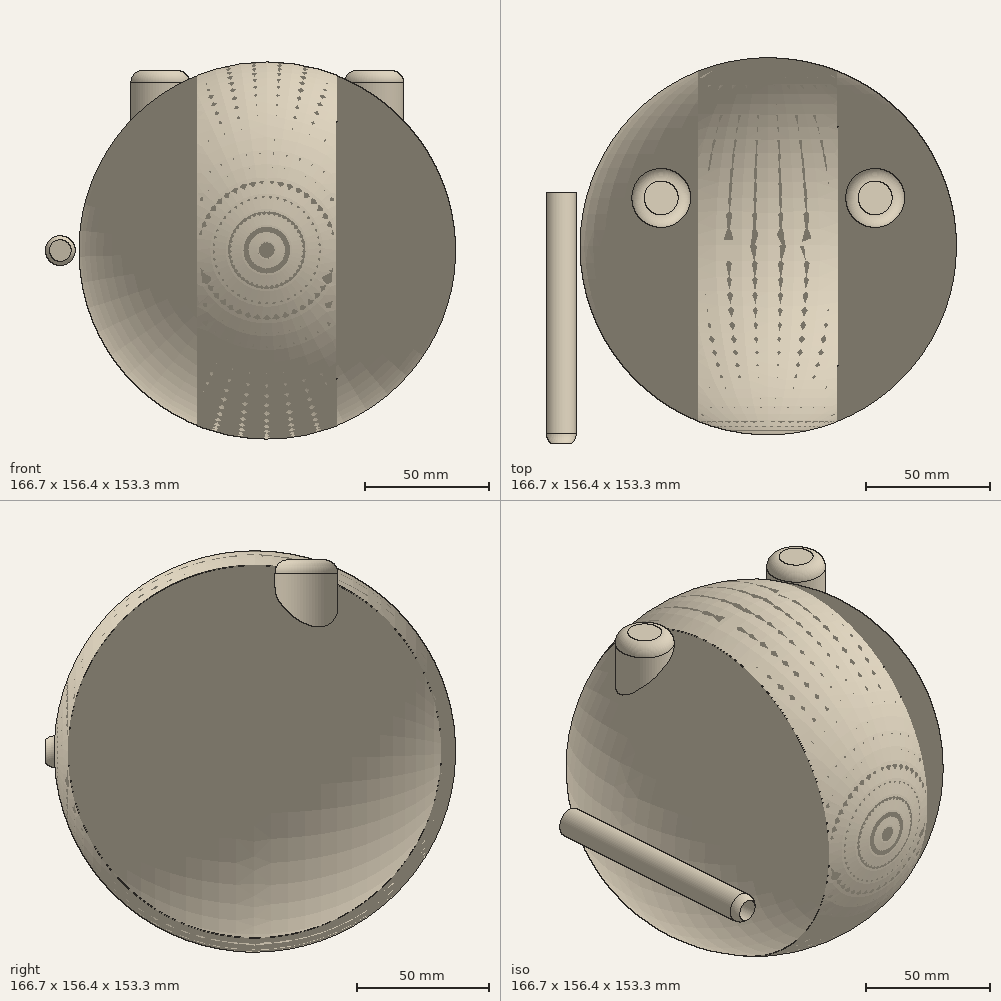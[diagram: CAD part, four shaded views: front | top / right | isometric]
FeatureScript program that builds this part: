
annotation { "Feature Type Name" : "Feature", "Feature Type Description" : "" }
export const myFeature = defineFeature(function(context is Context, id is Id, definition is map)
    precondition{}
    {
        {
            var Q0;
            Q0=qCreatedBy(makeId("Right.planeOp"),FACE);
            var sketch = newSketch(context, id + "F0", { "sketchPlane" : qUnion([Q0])});
            skLineSegment(sketch, "E0", {"start": v(-76.56, 0) * mm, "end": v(76.56, 0) * mm});
            skArc(sketch, "E1", {"start": v(76.56, 0) * mm, "mid": v(0, 76.63) * mm, "end": v(-76.56, 0) * mm});
            skSolve(sketch);
        }
        {
            var Q0;
            Q0=makeQuery(id+"F0.imprint","IMPRINT",FACE,{"disambiguationData":[TD([[makeQuery(id+"F0.imprint","IMPRINT",EDGE,{"derivedFrom":sQuery(id+"F0.wireOp",EDGE,"E0")}),1.0]])]});
            var Q1;
            Q1=sQuery(id+"F0.wireOp",EDGE,"E0");
            revolve(context, id + "F1", {"entities" : qUnion([Q0]), "axis" : qUnion([Q1]), "revolveType" : RevolveType.FULL});
        }
        {
            var Q0;
            Q0=qCreatedBy(makeId("Right.planeOp"),FACE);
            var sketch = newSketch(context, id + "F2", { "sketchPlane" : qUnion([Q0])});
            skCircle(sketch, "E2", {"center": v(0, 0) * mm, "radius": 71.19 * mm});
            skSolve(sketch);
        }
        {
            var Q0;
            Q0 = qSketchRegion(id + "F2", true);
            extrude(context, id + "F3", {"entities" : qUnion([Q0]), "operationType" : NewBodyOperationType.REMOVE, "endBound" : BoundingType.SYMMETRIC, "oppositeDirection" : true, "depth" : 195.07 * mm});
        }
        {
            var Q0;
            Q0=qCreatedBy(makeId("Right.planeOp"),FACE);
            var sketch = newSketch(context, id + "F4", { "sketchPlane" : qUnion([Q0])});
            skCircle(sketch, "E3.0", {"center": v(0, 0) * mm, "radius": 71.19 * mm});
            skCircle(sketch, "E4", {"center": v(0, 0) * mm, "radius": 71.16 * mm});
            skCircle(sketch, "E5", {"center": v(0, 0) * mm, "radius": 65.17 * mm});
            skSolve(sketch);
        }
        {
            var Q0;
            Q0=makeQuery(id+"F4.imprint","IMPRINT",FACE,{"disambiguationData":[TD([[makeQuery(id+"F4.imprint","IMPRINT",EDGE,{"derivedFrom":sQuery(id+"F4.wireOp",EDGE,"E4")}),1.0]])]});
            extrude(context, id + "F5", {"entities" : qUnion([Q0]), "endBound" : BoundingType.SYMMETRIC, "depth" : 56.5 * mm});
        }
        {
            var Q0;
            Q0=qCreatedBy(makeId("Right.planeOp"),FACE);
            var sketch = newSketch(context, id + "F6", { "sketchPlane" : qUnion([Q0])});
            skLineSegment(sketch, "E6", {"start": v(-76.44, 0) * mm, "end": v(76.44, 0) * mm});
            skArc(sketch, "E7", {"start": v(76.44, 0) * mm, "mid": v(0, 75.8) * mm, "end": v(-76.44, 0) * mm});
            skSolve(sketch);
        }
        {
            var Q0;
            Q0=makeQuery(id+"F6.imprint","IMPRINT",FACE,{"disambiguationData":[TD([[makeQuery(id+"F6.imprint","IMPRINT",EDGE,{"derivedFrom":sQuery(id+"F6.wireOp",EDGE,"E6")}),1.0]])]});
            var Q1;
            Q1=sQuery(id+"F6.wireOp",EDGE,"E6");
            revolve(context, id + "F7", {"entities" : qUnion([Q0]), "axis" : qUnion([Q1]), "revolveType" : RevolveType.FULL, "oppositeDirection" : true});
        }
        {
            var Q0;
            Q0=qCreatedBy(makeId("Right.planeOp"),FACE);
            var sketch = newSketch(context, id + "F8", { "sketchPlane" : qUnion([Q0])});
            skLineSegment(sketch, "E8", {"start": v(0, 0) * mm, "end": v(-36.95, 0) * mm});
            skLineSegment(sketch, "E9", {"start": v(-36.95, 0) * mm, "end": v(-36.95, 19.05) * mm});
            skLineSegment(sketch, "E10", {"start": v(-36.95, 19.05) * mm, "end": v(0, 19.05) * mm});
            skLineSegment(sketch, "E11", {"start": v(0, 19.05) * mm, "end": v(0, 0) * mm});
            skLineSegment(sketch, "E12", {"start": v(0, 0) * mm, "end": v(0, -19.05) * mm});
            skLineSegment(sketch, "E13", {"start": v(0, -19.05) * mm, "end": v(-36.95, -19.05) * mm});
            skLineSegment(sketch, "E14", {"start": v(-36.95, -19.05) * mm, "end": v(-36.95, 0) * mm});
            skArc(sketch, "E15", {"start": v(0, -19.05) * mm, "mid": v(44.13, 0) * mm, "end": v(0, 19.05) * mm});
            skSolve(sketch);
        }
        {
            var Q0;
            Q0 = qSketchRegion(id + "F8", true);
            extrude(context, id + "F9", {"entities" : qUnion([Q0]), "operationType" : NewBodyOperationType.ADD, "endBound" : BoundingType.SYMMETRIC, "depth" : 151.9 * mm});
        }
        {
            var Q0;
            {var subQ0=sQuery(id+"F8.wireOp",EDGE,"E14");var subQ1=sQuery(id+"F8.wireOp",EDGE,"E9");var subQ2=sQuery(id+"F8.wireOp",EDGE,"E10");Q0=makeQuery(id+"F9.boolean.opBoolean","SPLIT",EDGE,{"disambiguationData":[TD([makeQuery(id+"F9.opExtrude","CAP_FACE",FACE,{"disambiguationData":[OSD([subQ1,subQ2,sQuery(id+"F8.wireOp",EDGE,"E13"),subQ0,sQuery(id+"F8.wireOp",EDGE,"E15")])],"isStart":false})])],"derivedFrom":makeQuery(id+"F9.opExtrude","SWEPT_EDGE",EDGE,{"disambiguationData":[OSD([subQ1,subQ2])]})});}
            var Q1;
            {var subQ0=sQuery(id+"F8.wireOp",EDGE,"E14");var subQ1=sQuery(id+"F8.wireOp",EDGE,"E9");var subQ2=sQuery(id+"F8.wireOp",EDGE,"E13");Q1=makeQuery(id+"F9.boolean.opBoolean","SPLIT",EDGE,{"disambiguationData":[TD([makeQuery(id+"F9.opExtrude","CAP_FACE",FACE,{"disambiguationData":[OSD([subQ1,sQuery(id+"F8.wireOp",EDGE,"E10"),subQ2,subQ0,sQuery(id+"F8.wireOp",EDGE,"E15")])],"isStart":false})])],"derivedFrom":makeQuery(id+"F9.opExtrude","SWEPT_EDGE",EDGE,{"disambiguationData":[OSD([subQ2,subQ0])]})});}
            var Q2;
            Q2=makeQuery(id+"F9.opExtrude","CAP_EDGE",EDGE,{"disambiguationData":[OSD([sQuery(id+"F8.wireOp",EDGE,"E9"),sQuery(id+"F8.wireOp",EDGE,"E14")])],"isStart":false});
            var Q3;
            Q3=makeQuery(id+"F9.opExtrude","CAP_EDGE",EDGE,{"disambiguationData":[OSD([sQuery(id+"F8.wireOp",EDGE,"E13")])],"isStart":false});
            var Q4;
            Q4=makeQuery(id+"F9.opExtrude","CAP_EDGE",EDGE,{"disambiguationData":[OSD([sQuery(id+"F8.wireOp",EDGE,"E10")])],"isStart":false});
            var Q5;
            Q5=makeQuery(id+"F9.opExtrude","CAP_EDGE",EDGE,{"disambiguationData":[OSD([sQuery(id+"F8.wireOp",EDGE,"E15")])],"isStart":false});
            fillet(context, id + "F10", {"entities" : qUnion([Q0, Q1, Q2, Q3, Q4, Q5]), "radius" : 7.87 * mm, "tangentPropagation" : true, "allowEdgeOverflow" : false});
        }
        {
            var Q0;
            Q0=makeQuery(id+"F9.opExtrude","CAP_EDGE",EDGE,{"disambiguationData":[OSD([sQuery(id+"F8.wireOp",EDGE,"E9"),sQuery(id+"F8.wireOp",EDGE,"E14")])],"isStart":true});
            var Q1;
            {var subQ0=sQuery(id+"F8.wireOp",EDGE,"E14");var subQ1=sQuery(id+"F8.wireOp",EDGE,"E9");var subQ2=sQuery(id+"F8.wireOp",EDGE,"E10");Q1=makeQuery(id+"F9.boolean.opBoolean","SPLIT",EDGE,{"disambiguationData":[TD([makeQuery(id+"F9.opExtrude","CAP_FACE",FACE,{"disambiguationData":[OSD([subQ1,subQ2,sQuery(id+"F8.wireOp",EDGE,"E13"),subQ0,sQuery(id+"F8.wireOp",EDGE,"E15")])],"isStart":true})])],"derivedFrom":makeQuery(id+"F9.opExtrude","SWEPT_EDGE",EDGE,{"disambiguationData":[OSD([subQ1,subQ2])]})});}
            var Q2;
            {var subQ0=sQuery(id+"F8.wireOp",EDGE,"E14");var subQ1=sQuery(id+"F8.wireOp",EDGE,"E9");var subQ2=sQuery(id+"F8.wireOp",EDGE,"E13");Q2=makeQuery(id+"F9.boolean.opBoolean","SPLIT",EDGE,{"disambiguationData":[TD([makeQuery(id+"F9.opExtrude","CAP_FACE",FACE,{"disambiguationData":[OSD([subQ1,sQuery(id+"F8.wireOp",EDGE,"E10"),subQ2,subQ0,sQuery(id+"F8.wireOp",EDGE,"E15")])],"isStart":true})])],"derivedFrom":makeQuery(id+"F9.opExtrude","SWEPT_EDGE",EDGE,{"disambiguationData":[OSD([subQ2,subQ0])]})});}
            var Q3;
            Q3=makeQuery(id+"F9.opExtrude","CAP_EDGE",EDGE,{"disambiguationData":[OSD([sQuery(id+"F8.wireOp",EDGE,"E13")])],"isStart":true});
            var Q4;
            Q4=makeQuery(id+"F9.opExtrude","CAP_EDGE",EDGE,{"disambiguationData":[OSD([sQuery(id+"F8.wireOp",EDGE,"E10")])],"isStart":true});
            var Q5;
            Q5=makeQuery(id+"F9.opExtrude","CAP_EDGE",EDGE,{"disambiguationData":[OSD([sQuery(id+"F8.wireOp",EDGE,"E15")])],"isStart":true});
            fillet(context, id + "F11", {"entities" : qUnion([Q0, Q1, Q2, Q3, Q4, Q5]), "radius" : 7.87 * mm, "tangentPropagation" : true, "allowEdgeOverflow" : false});
        }
        {
            var Q0;
            Q0=makeQuery(id+"F9.opExtrude","CAP_FACE",FACE,{"disambiguationData":[OSD([sQuery(id+"F8.wireOp",EDGE,"E9"),sQuery(id+"F8.wireOp",EDGE,"E10"),sQuery(id+"F8.wireOp",EDGE,"E13"),sQuery(id+"F8.wireOp",EDGE,"E14"),sQuery(id+"F8.wireOp",EDGE,"E15")])],"isStart":false});
            var sketch = newSketch(context, id + "F12", { "sketchPlane" : qUnion([Q0])});
            skLineSegment(sketch, "E16", {"start": v(-29.07, 0) * mm, "end": v(36.26, 0) * mm});
            skLineSegment(sketch, "E17", {"start": v(0, 0) * mm, "end": v(0, 13.22) * mm});
            skLineSegment(sketch, "E18", {"start": v(0, 0) * mm, "end": v(0, -13.22) * mm});
            skArc(sketch, "E19", {"start": v(20.06, -18.18) * mm, "mid": v(36.26, 0) * mm, "end": v(20.06, 18.18) * mm});
            skLineSegment(sketch, "E20", {"start": v(20.06, 18.18) * mm, "end": v(20.06, -18.18) * mm});
            skSolve(sketch);
        }
        {
            var Q0;
            {var subQ0=sQuery(id+"F12.wireOp",EDGE,"E19");var subQ1=sQuery(id+"F12.wireOp",EDGE,"E16");var subQ2=makeQuery(id+"F12.imprint","INTERSECT",VERTEX,{"derivedFrom":[subQ1,subQ0]});Q0=makeQuery(id+"F12.imprint","IMPRINT",FACE,{"disambiguationData":[TD([[makeQuery(id+"F12.imprint","IMPRINT",EDGE,{"disambiguationData":[TD([[subQ2,1.0]])],"derivedFrom":subQ1}),1.0]])]});}
            var Q1;
            {var subQ0=sQuery(id+"F12.wireOp",EDGE,"E19");var subQ1=sQuery(id+"F12.wireOp",EDGE,"E16");var subQ2=makeQuery(id+"F12.imprint","INTERSECT",VERTEX,{"derivedFrom":[subQ1,subQ0]});Q1=makeQuery(id+"F12.imprint","IMPRINT",FACE,{"disambiguationData":[TD([[makeQuery(id+"F12.imprint","IMPRINT",EDGE,{"disambiguationData":[TD([[subQ2,1.0]])],"derivedFrom":subQ1}),-1.0]])]});}
            var Q2;
            Q2=sQuery(id+"F12.wireOp",EDGE,"E20");
            revolve(context, id + "F13", {"operationType" : NewBodyOperationType.ADD, "entities" : qUnion([Q0, Q1]), "axis" : qUnion([Q2]), "revolveType" : RevolveType.FULL});
        }
        {
            var Q0;
            Q0=makeQuery(id+"F9.opExtrude","CAP_FACE",FACE,{"disambiguationData":[OSD([sQuery(id+"F8.wireOp",EDGE,"E9"),sQuery(id+"F8.wireOp",EDGE,"E10"),sQuery(id+"F8.wireOp",EDGE,"E13"),sQuery(id+"F8.wireOp",EDGE,"E14"),sQuery(id+"F8.wireOp",EDGE,"E15")])],"isStart":true});
            var sketch = newSketch(context, id + "F14", { "sketchPlane" : qUnion([Q0])});
            skLineSegment(sketch, "E21", {"start": v(0, 0) * mm, "end": v(29.07, 0) * mm});
            skLineSegment(sketch, "E22", {"start": v(0, 0) * mm, "end": v(-36.26, 0) * mm});
            skLineSegment(sketch, "E23", {"start": v(0, 0) * mm, "end": v(0, -13.22) * mm});
            skLineSegment(sketch, "E24", {"start": v(0, 0) * mm, "end": v(0, 13.22) * mm});
            skArc(sketch, "E25", {"start": v(-20.06, 18.18) * mm, "mid": v(-36.26, 0) * mm, "end": v(-20.06, -18.18) * mm});
            skLineSegment(sketch, "E26", {"start": v(-20.06, 18.18) * mm, "end": v(-20.06, -18.18) * mm});
            skSolve(sketch);
        }
        {
            var Q0;
            {var subQ0=sQuery(id+"F14.wireOp",EDGE,"E25");var subQ1=sQuery(id+"F14.wireOp",EDGE,"E22");var subQ2=makeQuery(id+"F14.imprint","INTERSECT",VERTEX,{"derivedFrom":[subQ1,subQ0]});Q0=makeQuery(id+"F14.imprint","IMPRINT",FACE,{"disambiguationData":[TD([[makeQuery(id+"F14.imprint","IMPRINT",EDGE,{"disambiguationData":[TD([[subQ2,1.0]])],"derivedFrom":subQ1}),-1.0]])]});}
            var Q1;
            {var subQ0=sQuery(id+"F14.wireOp",EDGE,"E25");var subQ1=sQuery(id+"F14.wireOp",EDGE,"E22");var subQ2=makeQuery(id+"F14.imprint","INTERSECT",VERTEX,{"derivedFrom":[subQ1,subQ0]});Q1=makeQuery(id+"F14.imprint","IMPRINT",FACE,{"disambiguationData":[TD([[makeQuery(id+"F14.imprint","IMPRINT",EDGE,{"disambiguationData":[TD([[subQ2,1.0]])],"derivedFrom":subQ1}),1.0]])]});}
            var Q2;
            Q2=sQuery(id+"F14.wireOp",EDGE,"E26");
            revolve(context, id + "F15", {"operationType" : NewBodyOperationType.ADD, "entities" : qUnion([Q0, Q1]), "axis" : qUnion([Q2]), "revolveType" : RevolveType.FULL, "oppositeDirection" : true});
        }
        {
            var Q0;
            {var subQ0=sQuery(id+"F8.wireOp",EDGE,"E14");var subQ1=sQuery(id+"F8.wireOp",EDGE,"E13");var subQ2=sQuery(id+"F8.wireOp",EDGE,"E10");var subQ3=sQuery(id+"F8.wireOp",EDGE,"E9");Q0=makeQuery(id+"F9.boolean.opBoolean","SPLIT",FACE,{"disambiguationData":[TD([makeQuery(id+"F9.opExtrude","CAP_FACE",FACE,{"disambiguationData":[OSD([subQ3,subQ2,subQ1,subQ0,sQuery(id+"F8.wireOp",EDGE,"E15")])],"isStart":true})])],"derivedFrom":makeQuery(id+"F9.opExtrude","SWEPT_FACE",FACE,{"disambiguationData":[OSD([subQ3,subQ0])]})});}
            var sketch = newSketch(context, id + "F16", { "sketchPlane" : qUnion([Q0])});
            skLineSegment(sketch, "E27.0.0", {"start": v(-75.95, 18.18) * mm, "end": v(-75.95, -18.18) * mm});
            skLineSegment(sketch, "E27.0.1", {"start": v(-75.95, -18.18) * mm, "end": v(-75.95, 18.18) * mm});
            skLineSegment(sketch, "E28", {"start": v(-75.95, 0) * mm, "end": v(-92.04, 0) * mm});
            skPoint(sketch, "E28.endSnap0", {"position": v(-75.95, 0) * mm});
            skCircle(sketch, "E29", {"center": v(-84, 0) * mm, "radius": 6.29 * mm});
            skSolve(sketch);
        }
        {
            var Q0;
            {var subQ0=sQuery(id+"F16.wireOp",EDGE,"E29");var subQ1=sQuery(id+"F16.wireOp",EDGE,"E28");var subQ2=makeQuery(id+"F16.imprint","INTERSECT",VERTEX,{"disambiguationData":[OD(0.0)],"derivedFrom":[subQ1,subQ0]});Q0=makeQuery(id+"F16.imprint","IMPRINT",FACE,{"disambiguationData":[TD([[makeQuery(id+"F16.imprint","IMPRINT",EDGE,{"disambiguationData":[TD([[subQ2,1.0]])],"derivedFrom":subQ1}),-1.0]])]});}
            var Q1;
            {var subQ0=sQuery(id+"F16.wireOp",EDGE,"E29");var subQ1=sQuery(id+"F16.wireOp",EDGE,"E28");var subQ2=makeQuery(id+"F16.imprint","INTERSECT",VERTEX,{"disambiguationData":[OD(0.0)],"derivedFrom":[subQ1,subQ0]});Q1=makeQuery(id+"F16.imprint","IMPRINT",FACE,{"disambiguationData":[TD([[makeQuery(id+"F16.imprint","IMPRINT",EDGE,{"disambiguationData":[TD([[subQ2,1.0]])],"derivedFrom":subQ1}),1.0]])]});}
            extrude(context, id + "F17", {"entities" : qUnion([Q0, Q1]), "operationType" : NewBodyOperationType.REMOVE, "oppositeDirection" : true, "depth" : 58.67 * mm});
        }
        {
            var Q0;
            Q0=makeQuery(id+"F17.boolean.opBoolean","COPY",FACE,{"derivedFrom":makeQuery(id+"F17.opExtrude","CAP_FACE",FACE,{"disambiguationData":[OSD([sQuery(id+"F16.wireOp",EDGE,"E29")])],"isStart":false})});
            var sketch = newSketch(context, id + "F18", { "sketchPlane" : qUnion([Q0])});
            skCircle(sketch, "E30", {"center": v(-84, 0) * mm, "radius": 6.05 * mm});
            skSolve(sketch);
        }
        {
            var Q0;
            Q0=makeQuery(id+"F18.imprint","IMPRINT",FACE,{"disambiguationData":[TD([[makeQuery(id+"F18.imprint","IMPRINT",EDGE,{"derivedFrom":sQuery(id+"F18.wireOp",EDGE,"E30")}),1.0]])]});
            extrude(context, id + "F19", {"entities" : qUnion([Q0]), "depth" : 101.6 * mm});
        }
        {
            var Q0;
            {var subQ0=sQuery(id+"F8.wireOp",EDGE,"E14");var subQ1=sQuery(id+"F8.wireOp",EDGE,"E13");var subQ2=sQuery(id+"F8.wireOp",EDGE,"E10");var subQ3=sQuery(id+"F8.wireOp",EDGE,"E9");Q0=makeQuery(id+"F9.boolean.opBoolean","SPLIT",FACE,{"disambiguationData":[TD([makeQuery(id+"F9.opExtrude","CAP_FACE",FACE,{"disambiguationData":[OSD([subQ3,subQ2,subQ1,subQ0,sQuery(id+"F8.wireOp",EDGE,"E15")])],"isStart":false})])],"derivedFrom":makeQuery(id+"F9.opExtrude","SWEPT_FACE",FACE,{"disambiguationData":[OSD([subQ3,subQ0])]})});}
            var sketch = newSketch(context, id + "F20", { "sketchPlane" : qUnion([Q0])});
            skLineSegment(sketch, "E31.0.0", {"start": v(75.95, -18.18) * mm, "end": v(75.95, 18.18) * mm});
            skLineSegment(sketch, "E31.0.1", {"start": v(75.95, -18.18) * mm, "end": v(75.95, 18.18) * mm});
            skLineSegment(sketch, "E32", {"start": v(75.95, 0) * mm, "end": v(92.03, 0) * mm});
            skPoint(sketch, "E32.endSnap0", {"position": v(75.95, 0) * mm});
            skCircle(sketch, "E33", {"center": v(83.99, 0) * mm, "radius": 6.29 * mm});
            skSolve(sketch);
        }
        {
            var Q0;
            {var subQ0=sQuery(id+"F20.wireOp",EDGE,"E33");var subQ1=sQuery(id+"F20.wireOp",EDGE,"E32");var subQ2=makeQuery(id+"F20.imprint","INTERSECT",VERTEX,{"disambiguationData":[OD(0.0)],"derivedFrom":[subQ1,subQ0]});Q0=makeQuery(id+"F20.imprint","IMPRINT",FACE,{"disambiguationData":[TD([[makeQuery(id+"F20.imprint","IMPRINT",EDGE,{"disambiguationData":[TD([[subQ2,-1.0]])],"derivedFrom":subQ1}),1.0]])]});}
            var Q1;
            {var subQ0=sQuery(id+"F20.wireOp",EDGE,"E33");var subQ1=sQuery(id+"F20.wireOp",EDGE,"E32");var subQ2=makeQuery(id+"F20.imprint","INTERSECT",VERTEX,{"disambiguationData":[OD(0.0)],"derivedFrom":[subQ1,subQ0]});Q1=makeQuery(id+"F20.imprint","IMPRINT",FACE,{"disambiguationData":[TD([[makeQuery(id+"F20.imprint","IMPRINT",EDGE,{"disambiguationData":[TD([[subQ2,-1.0]])],"derivedFrom":subQ1}),-1.0]])]});}
            extrude(context, id + "F21", {"entities" : qUnion([Q0, Q1]), "operationType" : NewBodyOperationType.REMOVE, "oppositeDirection" : true, "depth" : 57.4 * mm});
        }
        {
            var Q0;
            Q0=makeQuery(id+"F19.opExtrude","CAP_FACE",FACE,{"disambiguationData":[OSD([sQuery(id+"F18.wireOp",EDGE,"E30")])],"isStart":false});
            var sketch = newSketch(context, id + "F22", { "sketchPlane" : qUnion([Q0])});
            skCircle(sketch, "E34", {"center": v(-84, 0) * mm, "radius": 4.4 * mm});
            skSolve(sketch);
        }
        {
            var Q0;
            Q0=makeQuery(id+"F22.imprint","IMPRINT",FACE,{"disambiguationData":[TD([[makeQuery(id+"F22.imprint","IMPRINT",EDGE,{"derivedFrom":sQuery(id+"F22.wireOp",EDGE,"E34")}),1.0]])]});
            extrude(context, id + "F23", {"entities" : qUnion([Q0]), "operationType" : NewBodyOperationType.REMOVE, "oppositeDirection" : true, "depth" : 95.5 * mm});
        }
        {
            var Q0;
            Q0=makeQuery(id+"F19.opExtrude","CAP_EDGE",EDGE,{"disambiguationData":[OSD([sQuery(id+"F18.wireOp",EDGE,"E30")])],"isStart":false});
            fillet(context, id + "F24", {"entities" : qUnion([Q0]), "radius" : 5.08 * mm, "tangentPropagation" : true, "allowEdgeOverflow" : false});
        }
        {
            var Q0;
            Q0=qCreatedBy(makeId("Front.planeOp"),FACE);
            var sketch = newSketch(context, id + "F25", { "sketchPlane" : qUnion([Q0])});
            skLineSegment(sketch, "E35", {"start": v(0, 0) * mm, "end": v(0, 76.34) * mm, "construction": true});
            skLineSegment(sketch, "E36", {"start": v(0, 0) * mm, "end": v(0, 38.17) * mm, "construction": true});
            skLineSegment(sketch, "E37", {"start": v(0, 38.17) * mm, "end": v(0, 19.08) * mm, "construction": true});
            skLineSegment(sketch, "E38", {"start": v(-30.36, 33.83) * mm, "end": v(-35.57, 33.83) * mm});
            skLineSegment(sketch, "E39", {"start": v(-35.57, 33.83) * mm, "end": v(-35.57, 28.63) * mm});
            skLineSegment(sketch, "E40", {"start": v(-30.36, 33.83) * mm, "end": v(-30.36, 28.63) * mm});
            skLineSegment(sketch, "E41", {"start": v(-30.36, 28.63) * mm, "end": v(-35.57, 28.63) * mm});
            skLineSegment(sketch, "E42", {"start": v(35.56, 28.63) * mm, "end": v(35.56, 33.83) * mm});
            skLineSegment(sketch, "E43", {"start": v(35.56, 33.83) * mm, "end": v(30.35, 33.83) * mm});
            skLineSegment(sketch, "E44", {"start": v(30.35, 33.83) * mm, "end": v(30.35, 28.63) * mm});
            skLineSegment(sketch, "E45", {"start": v(30.35, 28.63) * mm, "end": v(35.56, 28.63) * mm});
            skSolve(sketch);
        }
        {
            var Q0;
            Q0 = qSketchRegion(id + "F25", true);
            extrude(context, id + "F26", {"entities" : qUnion([Q0]), "operationType" : NewBodyOperationType.REMOVE, "depth" : 227.58 * mm});
        }
        {
            var Q0;
            Q0=qCreatedBy(makeId("Top.planeOp"),FACE);
            var sketch = newSketch(context, id + "F27", { "sketchPlane" : qUnion([Q0])});
            skLineSegment(sketch, "E46", {"start": v(0, 0) * mm, "end": v(0, 78.45) * mm, "construction": true});
            skLineSegment(sketch, "E47", {"start": v(0, 0) * mm, "end": v(0, 39.23) * mm, "construction": true});
            skLineSegment(sketch, "E48", {"start": v(0, 19.61) * mm, "end": v(-43.43, 19.61) * mm});
            skPoint(sketch, "E48.endSnap0", {"position": v(0, 19.61) * mm});
            skLineSegment(sketch, "E49", {"start": v(0, 19.61) * mm, "end": v(43.43, 19.61) * mm});
            skCircle(sketch, "E50", {"center": v(-43.43, 19.61) * mm, "radius": 12.9 * mm});
            skCircle(sketch, "E51", {"center": v(43.43, 19.61) * mm, "radius": 12.9 * mm});
            skSolve(sketch);
        }
        {
            var Q0;
            Q0 = qSketchRegion(id + "F27", true);
            extrude(context, id + "F28", {"entities" : qUnion([Q0]), "operationType" : NewBodyOperationType.REMOVE, "depth" : 80 * mm});
        }
        {
            var Q0;
            Q0=makeQuery(id+"F28.boolean.opBoolean","COPY",FACE,{"derivedFrom":makeQuery(id+"F28.opExtrude","CAP_FACE",FACE,{"disambiguationData":[OSD([sQuery(id+"F27.wireOp",EDGE,"E50")])],"isStart":true})});
            var sketch = newSketch(context, id + "F29", { "sketchPlane" : qUnion([Q0])});
            skCircle(sketch, "E52.0.0", {"center": v(43.43, 19.61) * mm, "radius": 12.9 * mm});
            skCircle(sketch, "E53.0.0", {"center": v(-43.43, 19.61) * mm, "radius": 12.9 * mm});
            skCircle(sketch, "E54", {"center": v(-43.43, 19.61) * mm, "radius": 12.29 * mm});
            skCircle(sketch, "E55", {"center": v(43.43, 19.61) * mm, "radius": 12.3 * mm});
            skSolve(sketch);
        }
        {
            var Q0;
            Q0=makeQuery(id+"F29.imprint","IMPRINT",FACE,{"disambiguationData":[TD([[makeQuery(id+"F29.imprint","IMPRINT",EDGE,{"derivedFrom":sQuery(id+"F29.wireOp",EDGE,"E54")}),1.0]])]});
            var Q1;
            Q1=makeQuery(id+"F29.imprint","IMPRINT",FACE,{"disambiguationData":[TD([[makeQuery(id+"F29.imprint","IMPRINT",EDGE,{"derivedFrom":sQuery(id+"F29.wireOp",EDGE,"E55")}),1.0]])]});
            extrude(context, id + "F30", {"entities" : qUnion([Q0, Q1]), "operationType" : NewBodyOperationType.ADD, "depth" : 45.72 * mm});
        }
        {
            var Q0;
            Q0=makeQuery(id+"F30.opExtrude","CAP_FACE",FACE,{"disambiguationData":[OSD([sQuery(id+"F29.wireOp",EDGE,"E54")])],"isStart":false});
            var sketch = newSketch(context, id + "F31", { "sketchPlane" : qUnion([Q0])});
            skCircle(sketch, "E56.0.0", {"center": v(-43.43, 19.61) * mm, "radius": 12.29 * mm});
            skCircle(sketch, "E57.0.0", {"center": v(43.43, 19.61) * mm, "radius": 12.3 * mm});
            skArc(sketch, "E58", {"start": v(-43.43, 7.33) * mm, "mid": v(-31.28, 19.61) * mm, "end": v(-43.43, 31.9) * mm});
            skArc(sketch, "E59", {"start": v(43.43, 31.9) * mm, "mid": v(31, 19.61) * mm, "end": v(43.43, 7.32) * mm});
            skSolve(sketch);
        }
        {
            var Q0;
            Q0=makeQuery(id+"F31.imprint","IMPRINT",FACE,{"disambiguationData":[TD([[makeQuery(id+"F31.imprint","IMPRINT",EDGE,{"derivedFrom":sQuery(id+"F31.wireOp",EDGE,"E58")}),1.0]])]});
            var Q1;
            {var subQ0=sQuery(id+"F31.wireOp",EDGE,"tqBclCao-ff7I-8XDz-RIih-4FscW2RvWS1z");Q1=makeQuery(id+"F31.imprint","IMPRINT",FACE,{"disambiguationData":[TD([[makeQuery(id+"F31.imprint","IMPRINT",EDGE,{"derivedFrom":subQ0}),-1.0]])]});}
            var Q2;
            {var subQ0=sQuery(id+"F31.wireOp",EDGE,"tqBclCao-ff7I-8XDz-RIih-4FscW2RvWS1z");Q2=makeQuery(id+"F31.imprint","IMPRINT",FACE,{"disambiguationData":[TD([[makeQuery(id+"F31.imprint","IMPRINT",EDGE,{"derivedFrom":subQ0}),1.0]])]});}
            var Q3;
            {var subQ0=sQuery(id+"F31.wireOp",EDGE,"CYRSiGfK-e9dC-9p3C-w0By-S7lAvkeTB2om");Q3=makeQuery(id+"F31.imprint","IMPRINT",FACE,{"disambiguationData":[TD([[makeQuery(id+"F31.imprint","IMPRINT",EDGE,{"derivedFrom":subQ0}),-1.0]])]});}
            extrude(context, id + "F32", {"entities" : qUnion([Q0, Q1, Q2, Q3]), "depth" : 24.9 * mm});
        }
        {
            var Q0;
            Q0=makeQuery(id+"F32.opExtrude","CAP_EDGE",EDGE,{"disambiguationData":[OSD([sQuery(id+"F31.wireOp",EDGE,"E58")])],"isStart":false});
            var Q1;
            Q1=makeQuery(id+"F32.opExtrude","CAP_EDGE",EDGE,{"disambiguationData":[OSD([sQuery(id+"F31.wireOp",EDGE,"E56.0.0")])],"isStart":false});
            var Q2;
            Q2=makeQuery(id+"F32.opExtrude","CAP_EDGE",EDGE,{"disambiguationData":[OSD([sQuery(id+"F31.wireOp",EDGE,"E57.0.0")])],"isStart":false});
            fillet(context, id + "F33", {"entities" : qUnion([Q0, Q1, Q2]), "radius" : 7.62 * mm, "tangentPropagation" : true, "allowEdgeOverflow" : false});
        }
        {
            var Q0;
            Q0=qCreatedBy(makeId("Front.planeOp"),FACE);
            var sketch = newSketch(context, id + "F34", { "sketchPlane" : qUnion([Q0])});
            skLineSegment(sketch, "E60", {"start": v(0, 74.25) * mm, "end": v(0, -74.03) * mm});
            skArc(sketch, "E61", {"start": v(0, -74.03) * mm, "mid": v(74.04, 0.11) * mm, "end": v(0, 74.25) * mm});
            skSolve(sketch);
        }
        {
            var Q0;
            Q0 = qSketchRegion(id + "F34", true);
            var Q1;
            Q1=sQuery(id+"F34.wireOp",EDGE,"E60");
            revolve(context, id + "F35", {"operationType" : NewBodyOperationType.REMOVE, "entities" : qUnion([Q0]), "axis" : qUnion([Q1]), "revolveType" : RevolveType.FULL, "oppositeDirection" : true});
        }
        {
            var Q0;
            Q0=qCreatedBy(makeId("Front.planeOp"),FACE);
            var sketch = newSketch(context, id + "F36", { "sketchPlane" : qUnion([Q0])});
            skLineSegment(sketch, "E62", {"start": v(0, 0) * mm, "end": v(0, -50.8) * mm});
            skLineSegment(sketch, "E63", {"start": v(0, -50.8) * mm, "end": v(25.4, -50.8) * mm});
            skLineSegment(sketch, "E64", {"start": v(0, -50.8) * mm, "end": v(-25.4, -50.8) * mm});
            skArc(sketch, "E65", {"start": v(-25.4, -50.8) * mm, "mid": v(0, -72.82) * mm, "end": v(25.4, -50.8) * mm});
            skLineSegment(sketch, "E66", {"start": v(0, -50.8) * mm, "end": v(0, 73.68) * mm});
            skArc(sketch, "E67", {"start": v(0, -72.82) * mm, "mid": v(72.82, 0.43) * mm, "end": v(0, 73.68) * mm});
            skSolve(sketch);
        }
        {
            var Q0;
            {var subQ1=sQuery(id+"F36.wireOp",EDGE,"E63");Q0=makeQuery(id+"F36.imprint","IMPRINT",FACE,{"disambiguationData":[TD([[makeQuery(id+"F36.imprint","IMPRINT",EDGE,{"derivedFrom":subQ1}),-1.0]])]});}
            var Q1;
            Q1=sQuery(id+"F36.wireOp",EDGE,"E63");
            revolve(context, id + "F37", {"entities" : qUnion([Q0]), "axis" : qUnion([Q1]), "revolveType" : RevolveType.SYMMETRIC, "angle" : 180 * degree});
        }
        {
            var Q0;
            Q0=qCreatedBy(makeId("Top.planeOp"),FACE);
            var sketch = newSketch(context, id + "F38", { "sketchPlane" : qUnion([Q0])});
            skCircle(sketch, "E68", {"center": v(-43.43, 19.61) * mm, "radius": 11.96 * mm});
            skCircle(sketch, "E69", {"center": v(43.43, 19.61) * mm, "radius": 11.96 * mm});
            skSolve(sketch);
        }
        {
            var Q0;
            Q0=makeQuery(id+"F32.opExtrude","SWEPT_BODY",BODY,{"disambiguationData":[OSD([sQuery(id+"F31.wireOp",EDGE,"E56.0.0"),sQuery(id+"F31.wireOp",EDGE,"E58")])]});
            deleteBodies(context, id + "F39", {"entities" : qUnion([Q0])});
        }
        {
            var Q0;
            Q0=makeQuery(id+"F35.boolean.opBoolean","SPLIT",BODY,{"disambiguationData":[OD(1.0)],"derivedFrom":makeQuery(id+"F7.opRevolve","SWEPT_BODY",BODY,{"disambiguationData":[OSD([sQuery(id+"F6.wireOp",EDGE,"E6"),sQuery(id+"F6.wireOp",EDGE,"E7")])]})});
            var Q1;
            Q1=makeQuery(id+"F35.boolean.opBoolean","SPLIT",BODY,{"disambiguationData":[OD(2.0)],"derivedFrom":makeQuery(id+"F7.opRevolve","SWEPT_BODY",BODY,{"disambiguationData":[OSD([sQuery(id+"F6.wireOp",EDGE,"E6"),sQuery(id+"F6.wireOp",EDGE,"E7")])]})});
            deleteBodies(context, id + "F40", {"entities" : qUnion([Q0, Q1])});
        }
        {
            var Q0;
            Q0=makeQuery(id+"F38.imprint","IMPRINT",FACE,{"disambiguationData":[TD([[makeQuery(id+"F38.imprint","IMPRINT",EDGE,{"derivedFrom":sQuery(id+"F38.wireOp",EDGE,"E68")}),1.0]])]});
            var Q1;
            Q1=makeQuery(id+"F38.imprint","IMPRINT",FACE,{"disambiguationData":[TD([[makeQuery(id+"F38.imprint","IMPRINT",EDGE,{"derivedFrom":sQuery(id+"F38.wireOp",EDGE,"E69")}),1.0]])]});
            extrude(context, id + "F41", {"entities" : qUnion([Q0, Q1]), "depth" : 73.15 * mm});
        }
        {
            var Q0;
            Q0=makeQuery(id+"F41.opExtrude","CAP_EDGE",EDGE,{"disambiguationData":[OSD([sQuery(id+"F38.wireOp",EDGE,"E68")])],"isStart":false});
            var Q1;
            Q1=makeQuery(id+"F41.opExtrude","CAP_EDGE",EDGE,{"disambiguationData":[OSD([sQuery(id+"F38.wireOp",EDGE,"E69")])],"isStart":false});
            fillet(context, id + "F42", {"entities" : qUnion([Q0, Q1]), "radius" : 5.08 * mm, "tangentPropagation" : true, "allowEdgeOverflow" : false});
        }
    });
